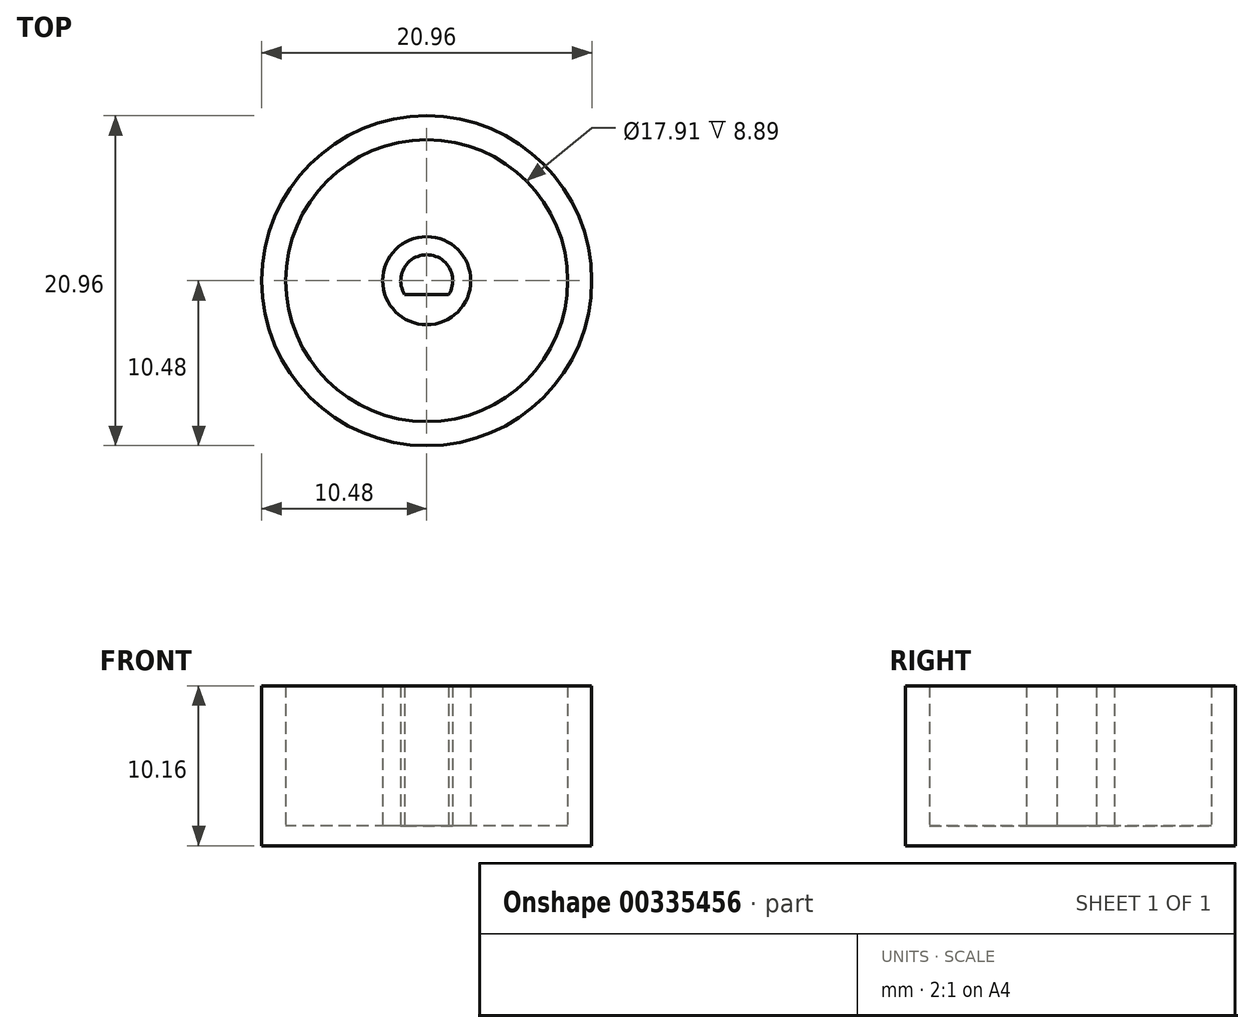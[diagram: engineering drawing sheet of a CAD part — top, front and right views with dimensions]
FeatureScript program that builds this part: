
annotation { "Feature Type Name" : "Feature", "Feature Type Description" : "" }
export const myFeature = defineFeature(function(context is Context, id is Id, definition is map)
    precondition{}
    {
        {
            var Q0;
            Q0=qCreatedBy(makeId("Top.planeOp"),FACE);
            var sketch = newSketch(context, id + "F0", { "sketchPlane" : qUnion([Q0])});
            skCircle(sketch, "E0", {"center": v(0, 0) * mm, "radius": 10.48 * mm});
            skSolve(sketch);
        }
        {
            var Q0;
            Q0=makeQuery(id+"F0.imprint","IMPRINT",FACE,{"disambiguationData":[TD([[makeQuery(id+"F0.imprint","IMPRINT",EDGE,{"derivedFrom":sQuery(id+"F0.wireOp",EDGE,"E0")}),1.0]])]});
            extrude(context, id + "F1", {"entities" : qUnion([Q0]), "depth" : 1.27 * mm});
        }
        {
            var Q0;
            Q0=makeQuery(id+"F1.opExtrude","CAP_FACE",FACE,{"disambiguationData":[OSD([sQuery(id+"F0.wireOp",EDGE,"E0")])],"isStart":false});
            var sketch = newSketch(context, id + "F2", { "sketchPlane" : qUnion([Q0])});
            skCircle(sketch, "E1", {"center": v(0, 0) * mm, "radius": 10.48 * mm});
            skCircle(sketch, "E2", {"center": v(0, 0) * mm, "radius": 8.95 * mm});
            skCircle(sketch, "E3", {"center": v(0, 0) * mm, "radius": 2.8 * mm});
            skArc(sketch, "E4", {"start": v(1.4, -0.88) * mm, "mid": v(0, 1.65) * mm, "end": v(-1.4, -0.88) * mm});
            skLineSegment(sketch, "E5", {"start": v(-1.4, -0.88) * mm, "end": v(1.4, -0.88) * mm});
            skSolve(sketch);
        }
        {
            var Q0;
            Q0=makeQuery(id+"F2.imprint","IMPRINT",FACE,{"disambiguationData":[TD([[makeQuery(id+"F2.imprint","IMPRINT",EDGE,{"derivedFrom":sQuery(id+"F2.wireOp",EDGE,"E1")}),1.0]])]});
            var Q1;
            Q1=makeQuery(id+"F2.imprint","IMPRINT",FACE,{"disambiguationData":[TD([[makeQuery(id+"F2.imprint","IMPRINT",EDGE,{"derivedFrom":sQuery(id+"F2.wireOp",EDGE,"E3")}),1.0]])]});
            extrude(context, id + "F3", {"entities" : qUnion([Q0, Q1]), "operationType" : NewBodyOperationType.ADD, "depth" : 8.9 * mm});
        }
        {
            var Q0;
            Q0=qCreatedBy(makeId("Front.planeOp"),FACE);
            var sketch = newSketch(context, id + "F4", { "sketchPlane" : qUnion([Q0])});
            skLineSegment(sketch, "E6.bottom", {"start": v(10.46, 5.17) * mm, "end": v(10.76, 5.17) * mm});
            skLineSegment(sketch, "E6.top", {"start": v(10.46, 2.12) * mm, "end": v(10.76, 2.12) * mm});
            skLineSegment(sketch, "E6.left", {"start": v(10.46, 5.17) * mm, "end": v(10.46, 2.12) * mm});
            skLineSegment(sketch, "E6.right", {"start": v(10.76, 5.17) * mm, "end": v(10.76, 2.12) * mm});
            skSolve(sketch);
        }
        {
            var Q0;
            Q0=sQuery(id+"F4.wireOp",EDGE,"E6.right");
            var Q1;
            Q1=makeQuery(id+"F3.boolean.opBoolean","MERGE",FACE,{"derivedFrom":[makeQuery(id+"F1.opExtrude","SWEPT_FACE",FACE,{"disambiguationData":[OSD([sQuery(id+"F0.wireOp",EDGE,"E0")])]}),makeQuery(id+"F3.opExtrude","SWEPT_FACE",FACE,{"disambiguationData":[OSD([sQuery(id+"F2.wireOp",EDGE,"E1")])]})]});
            revolve(context, id + "F5", {"bodyType" : ToolBodyType.SURFACE, "surfaceEntities" : qUnion([Q0]), "axis" : qUnion([Q1]), "revolveType" : RevolveType.FULL});
        }
    });
